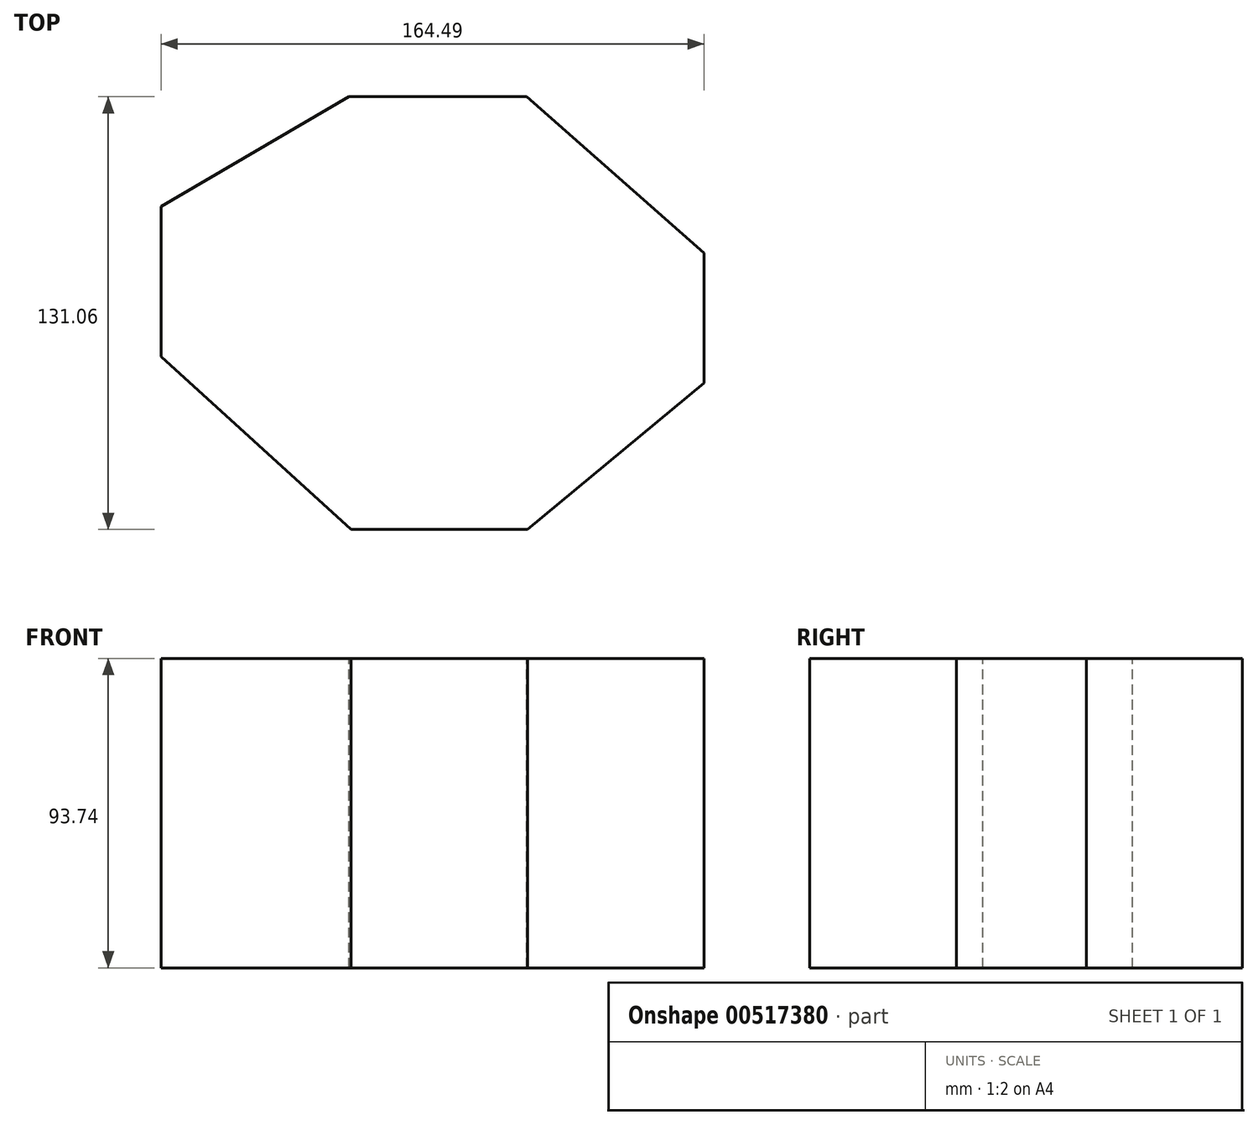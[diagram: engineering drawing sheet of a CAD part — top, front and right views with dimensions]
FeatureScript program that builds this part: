
annotation { "Feature Type Name" : "Feature", "Feature Type Description" : "" }
export const myFeature = defineFeature(function(context is Context, id is Id, definition is map)
    precondition{}
    {
        {
            var Q0;
            Q0=qCreatedBy(makeId("Front.planeOp"),FACE);
            var sketch = newSketch(context, id + "F0", { "sketchPlane" : qUnion([Q0])});
            skLineSegment(sketch, "E0.bottom", {"start": v(-65.73, 28.64) * mm, "end": v(98.76, 28.64) * mm});
            skLineSegment(sketch, "E0.top", {"start": v(-65.73, -65.1) * mm, "end": v(98.76, -65.1) * mm});
            skLineSegment(sketch, "E0.left", {"start": v(-65.73, 28.64) * mm, "end": v(-65.73, -65.1) * mm});
            skLineSegment(sketch, "E0.right", {"start": v(98.76, 28.64) * mm, "end": v(98.76, -65.1) * mm});
            skSolve(sketch);
        }
        {
            var Q0;
            Q0 = qSketchRegion(id + "F0", true);
            extrude(context, id + "F1", {"entities" : qUnion([Q0]), "depth" : 131.06 * mm, "offsetDistance" : 25.4 * mm});
        }
        {
            var Q0;
            Q0=makeQuery(id+"F1.opExtrude","SWEPT_FACE",FACE,{"disambiguationData":[OSD([sQuery(id+"F0.wireOp",EDGE,"E0.bottom")])]});
            var sketch = newSketch(context, id + "F2", { "sketchPlane" : qUnion([Q0])});
            skLineSegment(sketch, "E1", {"start": v(-65.73, -78.62) * mm, "end": v(-8.13, -131.06) * mm});
            skLineSegment(sketch, "E2", {"start": v(-8.13, -131.06) * mm, "end": v(44.82, -131.06) * mm});
            skLineSegment(sketch, "E3", {"start": v(44.82, -131.06) * mm, "end": v(98.76, -96.7) * mm});
            skLineSegment(sketch, "E4", {"start": v(98.76, -96.7) * mm, "end": v(98.76, -51.35) * mm});
            skLineSegment(sketch, "E5", {"start": v(98.76, -51.35) * mm, "end": v(41.3, 0) * mm});
            skLineSegment(sketch, "E6", {"start": v(41.3, 0) * mm, "end": v(-19.01, 0) * mm});
            skLineSegment(sketch, "E7", {"start": v(-19.01, 0) * mm, "end": v(-65.73, -25.09) * mm});
            skSolve(sketch);
        }
        {
            var Q0;
            Q0 = qSketchRegion(id + "F2", true);
            var Q1;
            {var subQ0=sQuery(id+"F2.wireOp",EDGE,"E1");Q1=makeQuery(id+"F2.imprint","IMPRINT",FACE,{"disambiguationData":[TD([[makeQuery(id+"F2.imprint","IMPRINT",EDGE,{"derivedFrom":subQ0}),-1.0]])]});}
            extrude(context, id + "F3", {"entities" : qUnion([Q0, Q1]), "operationType" : NewBodyOperationType.REMOVE, "oppositeDirection" : true, "depth" : 109.47 * mm, "offsetDistance" : 25.4 * mm});
        }
        {
            var Q0;
            Q0=makeQuery(id+"F1.opExtrude","SWEPT_FACE",FACE,{"disambiguationData":[OSD([sQuery(id+"F0.wireOp",EDGE,"E0.bottom")])]});
            var sketch = newSketch(context, id + "F4", { "sketchPlane" : qUnion([Q0])});
            skLineSegment(sketch, "E8", {"start": v(-65.73, -33.22) * mm, "end": v(-19.07, 0) * mm});
            skSolve(sketch);
        }
        {
            var Q0;
            {var subQ0=sQuery(id+"F4.wireOp",EDGE,"E8");Q0=makeQuery(id+"F4.imprint","IMPRINT",FACE,{"disambiguationData":[TD([[makeQuery(id+"F4.imprint","IMPRINT",EDGE,{"derivedFrom":subQ0}),1.0]])]});}
            extrude(context, id + "F5", {"entities" : qUnion([Q0]), "operationType" : NewBodyOperationType.REMOVE, "oppositeDirection" : true, "depth" : 175.77 * mm, "offsetDistance" : 25.4 * mm});
        }
        {
            var Q0;
            Q0=makeQuery(id+"F1.opExtrude","SWEPT_FACE",FACE,{"disambiguationData":[OSD([sQuery(id+"F0.wireOp",EDGE,"E0.bottom")])]});
            var sketch = newSketch(context, id + "F6", { "sketchPlane" : qUnion([Q0])});
            skLineSegment(sketch, "E9", {"start": v(-8.77, 0) * mm, "end": v(-65.73, -33.22) * mm});
            skSolve(sketch);
        }
        {
            var Q0;
            Q0 = qSketchRegion(id + "F6", true);
            var Q1;
            {var subQ0=sQuery(id+"F6.wireOp",EDGE,"E9");Q1=makeQuery(id+"F6.imprint","IMPRINT",FACE,{"disambiguationData":[TD([[makeQuery(id+"F6.imprint","IMPRINT",EDGE,{"derivedFrom":subQ0}),-1.0]])]});}
            extrude(context, id + "F7", {"entities" : qUnion([Q0, Q1]), "operationType" : NewBodyOperationType.REMOVE, "oppositeDirection" : true, "depth" : 175.5 * mm, "offsetDistance" : 25.4 * mm});
        }
        {
            var Q0;
            Q0=makeQuery(id+"F1.opExtrude","SWEPT_FACE",FACE,{"disambiguationData":[OSD([sQuery(id+"F0.wireOp",EDGE,"E0.bottom")])]});
            var sketch = newSketch(context, id + "F8", { "sketchPlane" : qUnion([Q0])});
            skLineSegment(sketch, "E10", {"start": v(45, 0) * mm, "end": v(98.76, -47.3) * mm});
            skLineSegment(sketch, "E11", {"start": v(98.76, -47.3) * mm, "end": v(98.76, -86.67) * mm});
            skLineSegment(sketch, "E12", {"start": v(98.76, -86.67) * mm, "end": v(45.31, -131.06) * mm});
            skSolve(sketch);
        }
        {
            var Q0;
            {var subQ0=sQuery(id+"F8.wireOp",EDGE,"E10");Q0=makeQuery(id+"F8.imprint","IMPRINT",FACE,{"disambiguationData":[TD([[makeQuery(id+"F8.imprint","IMPRINT",EDGE,{"derivedFrom":subQ0}),1.0]])]});}
            var Q1;
            {var subQ0=sQuery(id+"F8.wireOp",EDGE,"E12");Q1=makeQuery(id+"F8.imprint","IMPRINT",FACE,{"disambiguationData":[TD([[makeQuery(id+"F8.imprint","IMPRINT",EDGE,{"derivedFrom":subQ0}),1.0]])]});}
            extrude(context, id + "F9", {"entities" : qUnion([Q0, Q1]), "operationType" : NewBodyOperationType.REMOVE, "oppositeDirection" : true, "depth" : 113.54 * mm, "offsetDistance" : 25.4 * mm});
        }
    });
